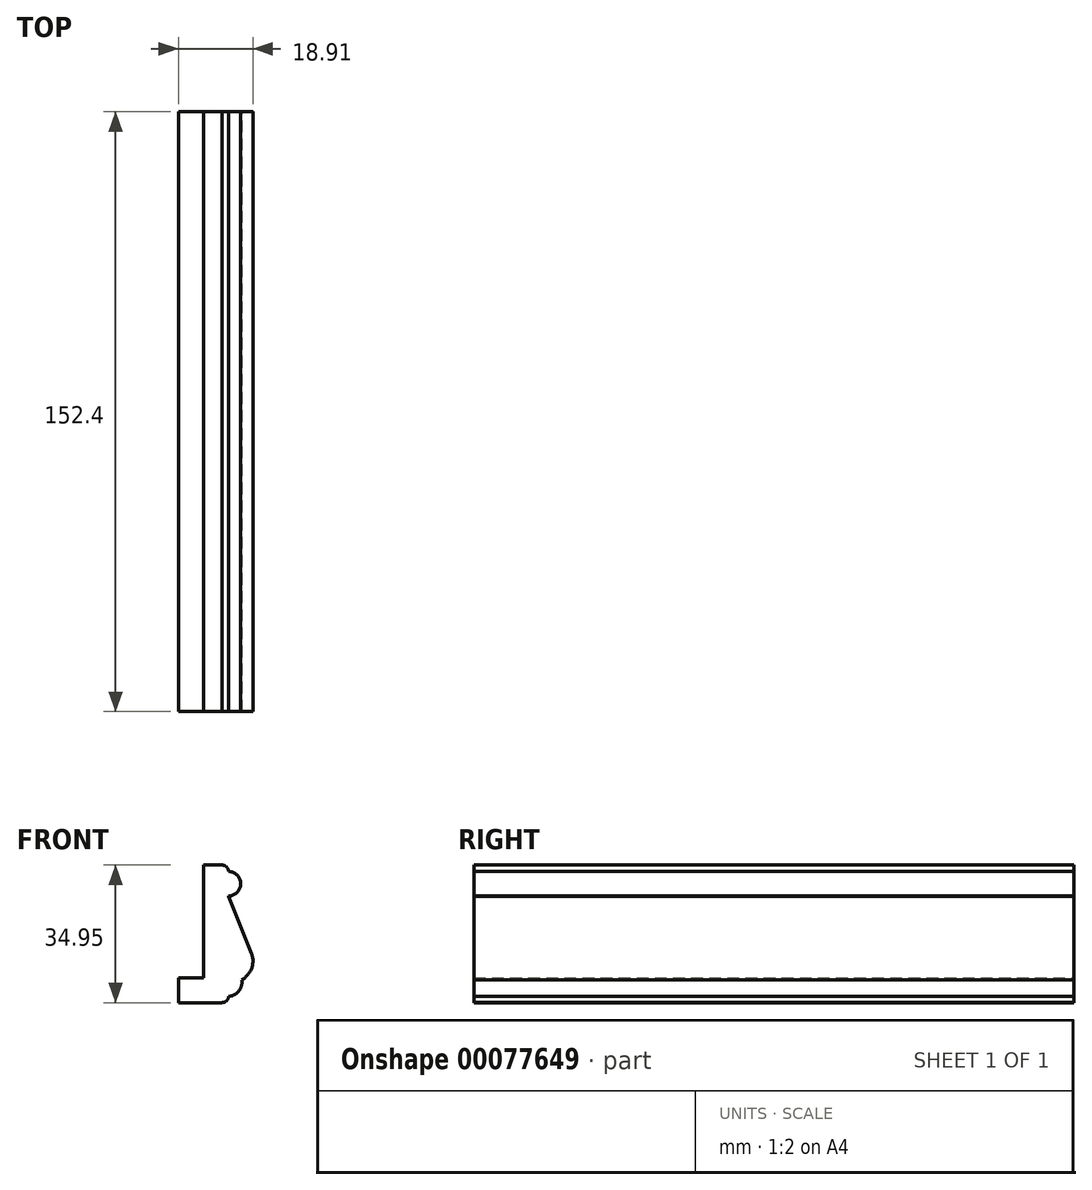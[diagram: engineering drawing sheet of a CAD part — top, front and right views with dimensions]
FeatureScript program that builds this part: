
annotation { "Feature Type Name" : "Feature", "Feature Type Description" : "" }
export const myFeature = defineFeature(function(context is Context, id is Id, definition is map)
    precondition{}
    {
        {
            var Q0;
            Q0=qCreatedBy(makeId("Front.planeOp"),FACE);
            var sketch = newSketch(context, id + "F0", { "sketchPlane" : qUnion([Q0])});
            skLineSegment(sketch, "E0", {"start": v(1.57, -24.24) * mm, "end": v(-9.54, -24.24) * mm});
            skLineSegment(sketch, "E1", {"start": v(-9.54, -24.24) * mm, "end": v(-9.54, -17.89) * mm});
            skLineSegment(sketch, "E2", {"start": v(-9.54, -17.89) * mm, "end": v(-3.18, -17.89) * mm});
            skLineSegment(sketch, "E3", {"start": v(-3.18, -17.89) * mm, "end": v(-3.18, 10.71) * mm});
            skLineSegment(sketch, "E4", {"start": v(-3.18, 10.71) * mm, "end": v(1.59, 10.71) * mm});
            skLineSegment(sketch, "E5", {"start": v(9.53, -13.12) * mm, "end": v(3.18, 2.76) * mm});
            skArc(sketch, "E6", {"start": v(1.59, 10.71) * mm, "mid": v(2.7, 10.23) * mm, "end": v(3.14, 9.1) * mm});
            skArc(sketch, "E7", {"start": v(3.14, 9.1) * mm, "mid": v(5.37, 8.16) * mm, "end": v(6.27, 5.92) * mm});
            skArc(sketch, "E8", {"start": v(6.27, 5.92) * mm, "mid": v(5.34, 3.74) * mm, "end": v(3.14, 2.84) * mm});
            skLineSegment(sketch, "E9", {"start": v(3.18, 2.76) * mm, "end": v(3.14, 2.84) * mm});
            skArc(sketch, "E10", {"start": v(9.53, -13.12) * mm, "mid": v(8.73, -16.2) * mm, "end": v(6.54, -18.5) * mm});
            skArc(sketch, "E11", {"start": v(6.54, -18.5) * mm, "mid": v(5.76, -21.3) * mm, "end": v(3.17, -22.64) * mm});
            skArc(sketch, "E12", {"start": v(3.17, -22.64) * mm, "mid": v(2.7, -23.76) * mm, "end": v(1.57, -24.2) * mm});
            skLineSegment(sketch, "E13", {"start": v(1.57, -24.2) * mm, "end": v(1.57, -24.24) * mm});
            skSolve(sketch);
        }
        {
            var Q0;
            Q0=makeQuery(id+"F0.imprint","IMPRINT",FACE,{"disambiguationData":[TD([[makeQuery(id+"F0.imprint","IMPRINT",EDGE,{"derivedFrom":sQuery(id+"F0.wireOp",EDGE,"E0")}),-1.0]])]});
            extrude(context, id + "F1", {"entities" : qUnion([Q0]), "depth" : 152.4 * mm});
        }
        {
            var Q0;
            Q0=makeQuery(id+"F1.opExtrude","SWEPT_EDGE",EDGE,{"disambiguationData":[OSD([sQuery(id+"F0.wireOp",EDGE,"E5"),sQuery(id+"F0.wireOp",EDGE,"E10")])]});
            fillet(context, id + "F2", {"entities" : qUnion([Q0]), "radius" : 5.08 * mm, "tangentPropagation" : true, "allowEdgeOverflow" : false});
        }
    });
